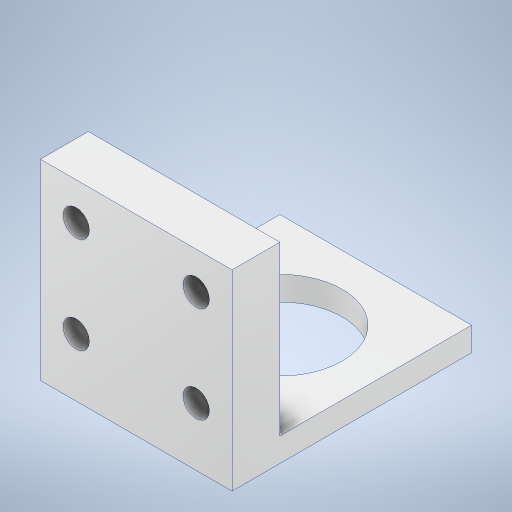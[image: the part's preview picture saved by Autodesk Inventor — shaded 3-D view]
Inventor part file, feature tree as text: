
AUTODESK INVENTOR PART (.ipt)
format: ipt  version: 2023 (Build 270158000, 158)  size: 266,240 bytes
history: native  units: mm
features: sketch x4, extrude x2, hole x2, other x1
ambient origin geometry x8: Origin, YZ Plane, XZ Plane, XY Plane, X Axis, Y Axis, Z Axis, Center Point
bodies: Body1 (feature_tree)
feature tree (9):
  other  "Sólido1"
  extrude  "Extrusão1"  Depth=50.0mm
  extrude  "Extrusão2"  Depth=10.0mm
  hole  "Furo1"  [1 undecoded]
  hole  "Hole2"  [1 undecoded]
  sketch  "Esboço1"  dims[d0=40.0mm d1=50.0mm]
  sketch  "Esboço2"  dims[d2=5.0mm d3=0.0mm d4=10.0mm]
  sketch  "Esboço3"  dims[d5=35.0mm d6=0.0mm d7=40.0mm]
  sketch  "Sketch4"  dims[d8=40.0mm d9=20.0mm d10=20.0mm d11=26.0mm d12=6.0mm d13=4.0mm d14=2.0mm d15=90.0deg d16=0.5mm d17=20.594885mm d18=20.0mm d20=20.1mm d21=20.0mm d23=25.05mm d26=7.75mm d27=40.0mm d28=7.475mm d29=5.5mm d30=4.0mm d31=4.0mm d32=2.0mm d33=90.0deg d34=0.5mm d35=20.594885mm]
note: 2 required parameter values undecoded (feature->parameter linkage not recoverable at this tier; creation-order binding heuristic only, values carry confidence <= 0.55)
